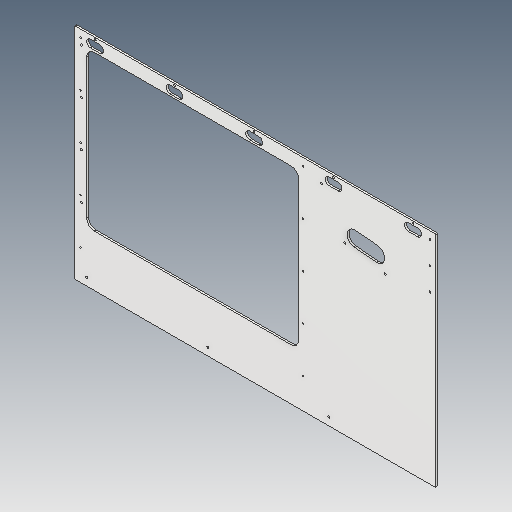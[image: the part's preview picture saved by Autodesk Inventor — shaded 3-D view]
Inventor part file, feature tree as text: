
AUTODESK INVENTOR PART (.ipt)
format: ipt  version: 2023.5 (Build 275446000, 446)  size: 148,992 bytes
history: native  units: in
note: dims shown in document units (in); Inventor stores cm internally (conversion verified against a paired STEP export)
features: fillet x1
ambient origin geometry x8: Origin, YZ Plane, XZ Plane, XY Plane, X Axis, Y Axis, Z Axis, Center Point
bodies: Solid1 (feature_tree)
feature tree (1):
  fillet  "Fillet2"  [1 undecoded]
note: 1 required parameter value undecoded (feature->parameter linkage not recoverable at this tier; creation-order binding heuristic only, values carry confidence <= 0.55)
